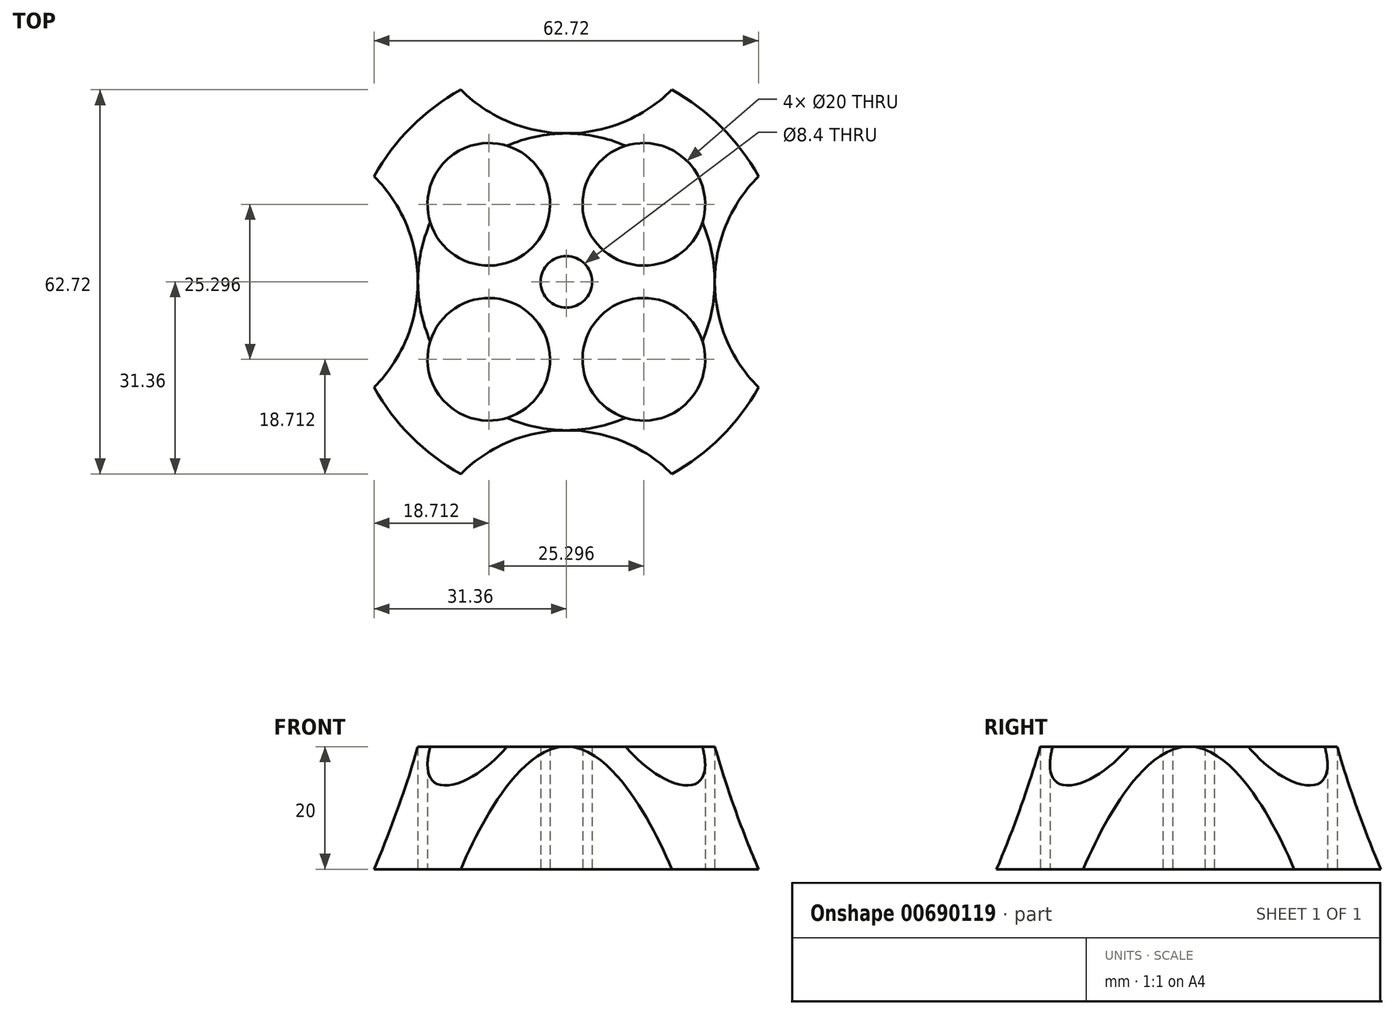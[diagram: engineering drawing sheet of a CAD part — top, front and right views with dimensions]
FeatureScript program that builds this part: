
annotation { "Feature Type Name" : "Feature", "Feature Type Description" : "" }
export const myFeature = defineFeature(function(context is Context, id is Id, definition is map)
    precondition{}
    {
        {
            var Q0;
            Q0=qCreatedBy(makeId("Front.planeOp"),FACE);
            var sketch = newSketch(context, id + "F0", { "sketchPlane" : qUnion([Q0])});
            skLineSegment(sketch, "E0", {"start": v(0, 0) * mm, "end": v(0, 20) * mm, "construction": true});
            skLineSegment(sketch, "E1", {"start": v(0, 20) * mm, "end": v(-24.23, 20) * mm});
            skLineSegment(sketch, "E2", {"start": v(-24.23, 20) * mm, "end": v(-35.77, 0) * mm});
            skLineSegment(sketch, "E3", {"start": v(-35.77, 0) * mm, "end": v(0, 0) * mm});
            skLineSegment(sketch, "E4", {"start": v(0, 10) * mm, "end": v(-30, 10) * mm, "construction": true});
            skLineSegment(sketch, "E5", {"start": v(-4.2, 20) * mm, "end": v(-4.2, 0) * mm});
            skSolve(sketch);
        }
        {
            var Q0;
            {var subQ0=sQuery(id+"F0.wireOp",EDGE,"E2");Q0=makeQuery(id+"F0.imprint","IMPRINT",FACE,{"disambiguationData":[TD([[makeQuery(id+"F0.imprint","IMPRINT",EDGE,{"derivedFrom":subQ0}),1.0]])]});}
            var Q1;
            Q1=sQuery(id+"F0.wireOp",EDGE,"E0");
            revolve(context, id + "F1", {"entities" : qUnion([Q0]), "axis" : qUnion([Q1]), "revolveType" : RevolveType.FULL});
        }
        {
            var Q0;
            Q0=qCreatedBy(makeId("Top.planeOp"),FACE);
            var sketch = newSketch(context, id + "F2", { "sketchPlane" : qUnion([Q0])});
            skCircle(sketch, "E6.0", {"center": v(0, 0) * mm, "radius": 35.77 * mm});
            skArc(sketch, "E7", {"start": v(-31.36, -17.22) * mm, "mid": v(-24.23, 0) * mm, "end": v(-31.36, 17.22) * mm});
            skLineSegment(sketch, "E8", {"start": v(-31.36, 17.22) * mm, "end": v(-14.14, 0) * mm, "construction": true});
            skLineSegment(sketch, "E9", {"start": v(-14.14, 0) * mm, "end": v(0, 0) * mm, "construction": true});
            skArc(sketch, "E10.1.0", {"start": v(17.22, -31.36) * mm, "mid": v(0, -24.23) * mm, "end": v(-17.22, -31.36) * mm});
            skArc(sketch, "E10.2.0", {"start": v(31.36, 17.22) * mm, "mid": v(24.23, 0) * mm, "end": v(31.36, -17.22) * mm});
            skArc(sketch, "E10.3.0", {"start": v(-17.22, 31.36) * mm, "mid": v(0, 24.23) * mm, "end": v(17.22, 31.36) * mm});
            skSolve(sketch);
        }
        {
            var Q0;
            {var subQ0=sQuery(id+"F2.wireOp",EDGE,"E10.3.0");Q0=makeQuery(id+"F2.imprint","IMPRINT",FACE,{"disambiguationData":[TD([[makeQuery(id+"F2.imprint","IMPRINT",EDGE,{"derivedFrom":subQ0}),1.0]])]});}
            var Q1;
            {var subQ0=sQuery(id+"F2.wireOp",EDGE,"E10.2.0");Q1=makeQuery(id+"F2.imprint","IMPRINT",FACE,{"disambiguationData":[TD([[makeQuery(id+"F2.imprint","IMPRINT",EDGE,{"derivedFrom":subQ0}),1.0]])]});}
            var Q2;
            {var subQ0=sQuery(id+"F2.wireOp",EDGE,"E10.1.0");Q2=makeQuery(id+"F2.imprint","IMPRINT",FACE,{"disambiguationData":[TD([[makeQuery(id+"F2.imprint","IMPRINT",EDGE,{"derivedFrom":subQ0}),1.0]])]});}
            var Q3;
            {var subQ0=sQuery(id+"F2.wireOp",EDGE,"E7");Q3=makeQuery(id+"F2.imprint","IMPRINT",FACE,{"disambiguationData":[TD([[makeQuery(id+"F2.imprint","IMPRINT",EDGE,{"derivedFrom":subQ0}),1.0]])]});}
            extrude(context, id + "F3", {"entities" : qUnion([Q0, Q1, Q2, Q3]), "operationType" : NewBodyOperationType.REMOVE, "endBound" : BoundingType.THROUGH_ALL, "depth" : 25 * mm});
        }
        {
            var Q0;
            Q0=qCreatedBy(makeId("Top.planeOp"),FACE);
            var sketch = newSketch(context, id + "F4", { "sketchPlane" : qUnion([Q0])});
            skCircle(sketch, "E11", {"center": v(-12.65, -12.65) * mm, "radius": 10 * mm});
            skCircle(sketch, "E12", {"center": v(12.65, -12.65) * mm, "radius": 10 * mm});
            skCircle(sketch, "E13", {"center": v(12.65, 12.65) * mm, "radius": 10 * mm});
            skCircle(sketch, "E14", {"center": v(-12.65, 12.65) * mm, "radius": 10 * mm});
            skLineSegment(sketch, "E15.bottom", {"start": v(-12.65, 12.65) * mm, "end": v(12.65, 12.65) * mm, "construction": true});
            skLineSegment(sketch, "E15.top", {"start": v(-12.65, -12.65) * mm, "end": v(12.65, -12.65) * mm, "construction": true});
            skLineSegment(sketch, "E15.left", {"start": v(-12.65, 12.65) * mm, "end": v(-12.65, -12.65) * mm, "construction": true});
            skLineSegment(sketch, "E15.right", {"start": v(12.65, 12.65) * mm, "end": v(12.65, -12.65) * mm, "construction": true});
            skPoint(sketch, "E15.middle", {"position": v(0, 0) * mm});
            skLineSegment(sketch, "E16", {"start": v(-12.65, 12.65) * mm, "end": v(-25.3, 25.3) * mm, "construction": true});
            skLineSegment(sketch, "E17", {"start": v(-12.65, 12.65) * mm, "end": v(0, 0) * mm, "construction": true});
            skSolve(sketch);
        }
        {
            var Q0;
            Q0=qSketchRegion(id+"F4",true);
            extrude(context, id + "F5", {"entities" : qUnion([Q0]), "operationType" : NewBodyOperationType.REMOVE, "endBound" : BoundingType.THROUGH_ALL, "depth" : 25 * mm});
        }
    });
